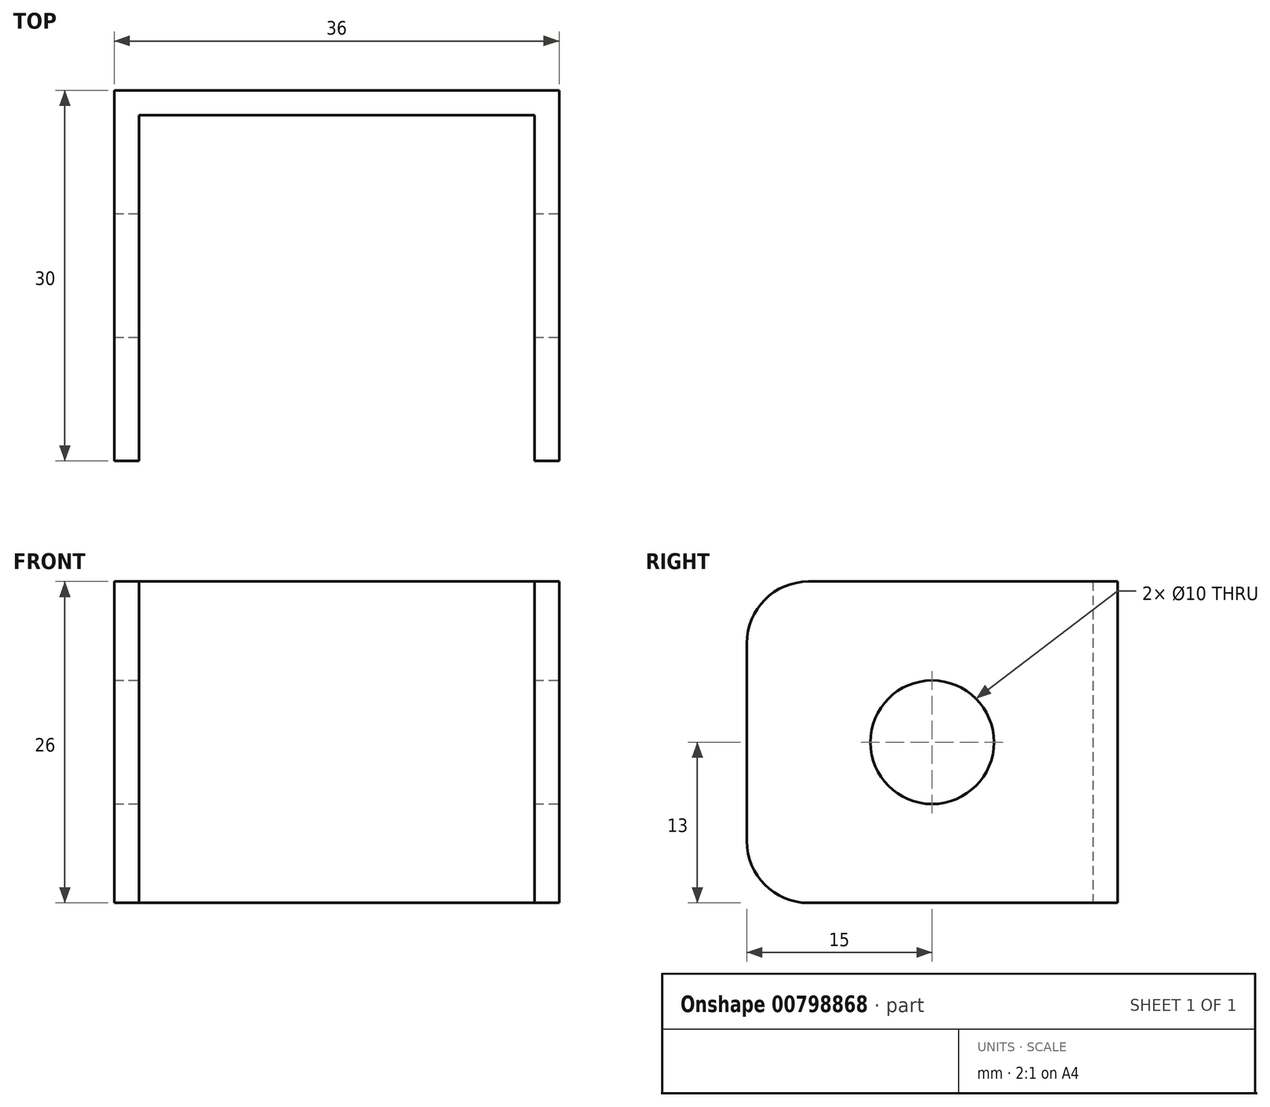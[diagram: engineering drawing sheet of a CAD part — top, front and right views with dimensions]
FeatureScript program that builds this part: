
annotation { "Feature Type Name" : "Feature", "Feature Type Description" : "" }
export const myFeature = defineFeature(function(context is Context, id is Id, definition is map)
    precondition{}
    {
        {
            var Q0;
            Q0=qCreatedBy(makeId("Front.planeOp"),FACE);
            var sketch = newSketch(context, id + "F0", { "sketchPlane" : qUnion([Q0])});
            skLineSegment(sketch, "E0.bottom", {"start": v(18, 13) * mm, "end": v(-18, 13) * mm});
            skLineSegment(sketch, "E0.top", {"start": v(18, -13) * mm, "end": v(-18, -13) * mm});
            skLineSegment(sketch, "E0.left", {"start": v(18, 13) * mm, "end": v(18, -13) * mm});
            skLineSegment(sketch, "E0.right", {"start": v(-18, 13) * mm, "end": v(-18, -13) * mm});
            skPoint(sketch, "E0.middle", {"position": v(0, 0) * mm});
            skSolve(sketch);
        }
        {
            var Q0;
            Q0 = qSketchRegion(id + "F0", true);
            extrude(context, id + "F1", {"entities" : qUnion([Q0]), "depth" : 30 * mm, "offsetDistance" : 25 * mm});
        }
        {
            var Q0;
            Q0=makeQuery(id+"F1.opExtrude","SWEPT_FACE",FACE,{"disambiguationData":[OSD([sQuery(id+"F0.wireOp",EDGE,"E0.top")])]});
            var sketch = newSketch(context, id + "F2", { "sketchPlane" : qUnion([Q0])});
            skLineSegment(sketch, "E1", {"start": v(-16, 30) * mm, "end": v(-16, 2) * mm});
            skLineSegment(sketch, "E2", {"start": v(-16, 2) * mm, "end": v(16, 2) * mm});
            skLineSegment(sketch, "E3", {"start": v(16, 2) * mm, "end": v(16, 30) * mm});
            skSolve(sketch);
        }
        {
            var Q0;
            Q0 = qSketchRegion(id + "F2", true);
            var Q1;
            {var subQ0=sQuery(id+"F2.wireOp",EDGE,"E1");Q1=makeQuery(id+"F2.imprint","IMPRINT",FACE,{"disambiguationData":[TD([[makeQuery(id+"F2.imprint","IMPRINT",EDGE,{"derivedFrom":subQ0}),1.0]])]});}
            extrude(context, id + "F3", {"entities" : qUnion([Q0, Q1]), "operationType" : NewBodyOperationType.REMOVE, "oppositeDirection" : true, "depth" : 36 * mm, "offsetDistance" : 25 * mm});
        }
        {
            var Q0;
            Q0=makeQuery(id+"F1.opExtrude","SWEPT_FACE",FACE,{"disambiguationData":[OSD([sQuery(id+"F0.wireOp",EDGE,"E0.left")])]});
            var sketch = newSketch(context, id + "F4", { "sketchPlane" : qUnion([Q0])});
            skCircle(sketch, "E4", {"center": v(-15, 0) * mm, "radius": 5 * mm});
            skPoint(sketch, "E4.centerSnap0", {"position": v(-15, -13) * mm});
            skSolve(sketch);
        }
        {
            var Q0;
            Q0 = qSketchRegion(id + "F4", true);
            extrude(context, id + "F5", {"entities" : qUnion([Q0]), "operationType" : NewBodyOperationType.REMOVE, "endBound" : BoundingType.THROUGH_ALL, "oppositeDirection" : true, "depth" : 25 * mm, "offsetDistance" : 25 * mm});
        }
        {
            var Q0;
            {var subQ0=sQuery(id+"F0.wireOp",EDGE,"E0.right");var subQ1=sQuery(id+"F0.wireOp",EDGE,"E0.top");Q0=makeQuery(id+"F3.boolean.opBoolean","SPLIT",EDGE,{"disambiguationData":[TD([makeQuery(id+"F1.opExtrude","SWEPT_FACE",FACE,{"disambiguationData":[OSD([subQ0])]})])],"derivedFrom":makeQuery(id+"F1.opExtrude","CAP_EDGE",EDGE,{"disambiguationData":[OSD([subQ1])],"isStart":false})});}
            var Q1;
            {var subQ0=sQuery(id+"F0.wireOp",EDGE,"E0.bottom");var subQ1=sQuery(id+"F0.wireOp",EDGE,"E0.right");Q1=makeQuery(id+"F3.boolean.opBoolean","SPLIT",EDGE,{"disambiguationData":[TD([makeQuery(id+"F1.opExtrude","SWEPT_FACE",FACE,{"disambiguationData":[OSD([subQ1])]})])],"derivedFrom":makeQuery(id+"F1.opExtrude","CAP_EDGE",EDGE,{"disambiguationData":[OSD([subQ0])],"isStart":false})});}
            var Q2;
            {var subQ0=sQuery(id+"F0.wireOp",EDGE,"E0.bottom");var subQ1=sQuery(id+"F0.wireOp",EDGE,"E0.left");Q2=makeQuery(id+"F3.boolean.opBoolean","SPLIT",EDGE,{"disambiguationData":[TD([makeQuery(id+"F1.opExtrude","SWEPT_FACE",FACE,{"disambiguationData":[OSD([subQ1])]})])],"derivedFrom":makeQuery(id+"F1.opExtrude","CAP_EDGE",EDGE,{"disambiguationData":[OSD([subQ0])],"isStart":false})});}
            var Q3;
            {var subQ0=sQuery(id+"F0.wireOp",EDGE,"E0.left");var subQ1=sQuery(id+"F0.wireOp",EDGE,"E0.top");Q3=makeQuery(id+"F3.boolean.opBoolean","SPLIT",EDGE,{"disambiguationData":[TD([makeQuery(id+"F1.opExtrude","SWEPT_FACE",FACE,{"disambiguationData":[OSD([subQ0])]})])],"derivedFrom":makeQuery(id+"F1.opExtrude","CAP_EDGE",EDGE,{"disambiguationData":[OSD([subQ1])],"isStart":false})});}
            fillet(context, id + "F6", {"entities" : qUnion([Q0, Q1, Q2, Q3]), "radius" : 5 * mm, "tangentPropagation" : true, "allowEdgeOverflow" : false});
        }
    });
